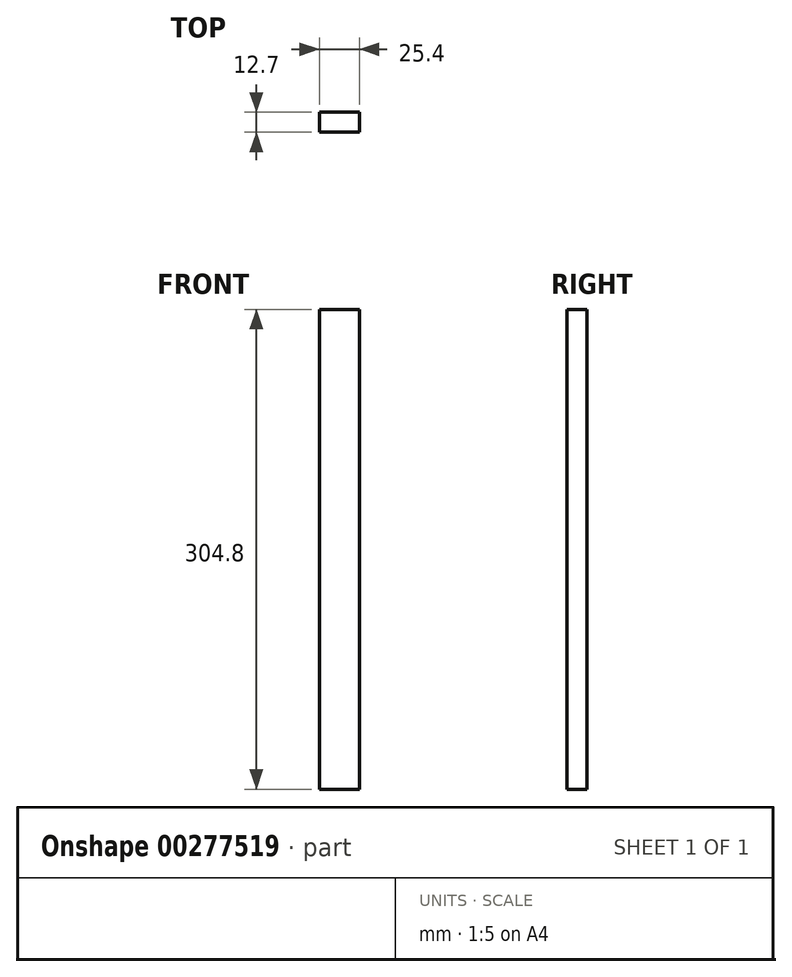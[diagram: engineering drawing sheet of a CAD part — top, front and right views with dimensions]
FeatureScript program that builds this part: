
annotation { "Feature Type Name" : "Feature", "Feature Type Description" : "" }
export const myFeature = defineFeature(function(context is Context, id is Id, definition is map)
    precondition{}
    {
        {
            var Q0;
            Q0=qCreatedBy(makeId("Top.planeOp"),FACE);
            var sketch = newSketch(context, id + "F0", { "sketchPlane" : qUnion([Q0])});
            skLineSegment(sketch, "E0.bottom", {"start": v(-12.7, 6.35) * mm, "end": v(12.7, 6.35) * mm});
            skLineSegment(sketch, "E0.top", {"start": v(-12.7, -6.35) * mm, "end": v(12.7, -6.35) * mm});
            skLineSegment(sketch, "E0.left", {"start": v(-12.7, 6.35) * mm, "end": v(-12.7, -6.35) * mm});
            skLineSegment(sketch, "E0.right", {"start": v(12.7, 6.35) * mm, "end": v(12.7, -6.35) * mm});
            skPoint(sketch, "E0.middle", {"position": v(0, 0) * mm});
            skSolve(sketch);
        }
        {
            var Q0;
            Q0=makeQuery(id+"F0.imprint","IMPRINT",FACE,{"disambiguationData":[TD([[makeQuery(id+"F0.imprint","IMPRINT",EDGE,{"derivedFrom":sQuery(id+"F0.wireOp",EDGE,"E0.bottom")}),-1.0]])]});
            extrude(context, id + "F1", {"entities" : qUnion([Q0]), "depth" : 304.8 * mm});
        }
    });
